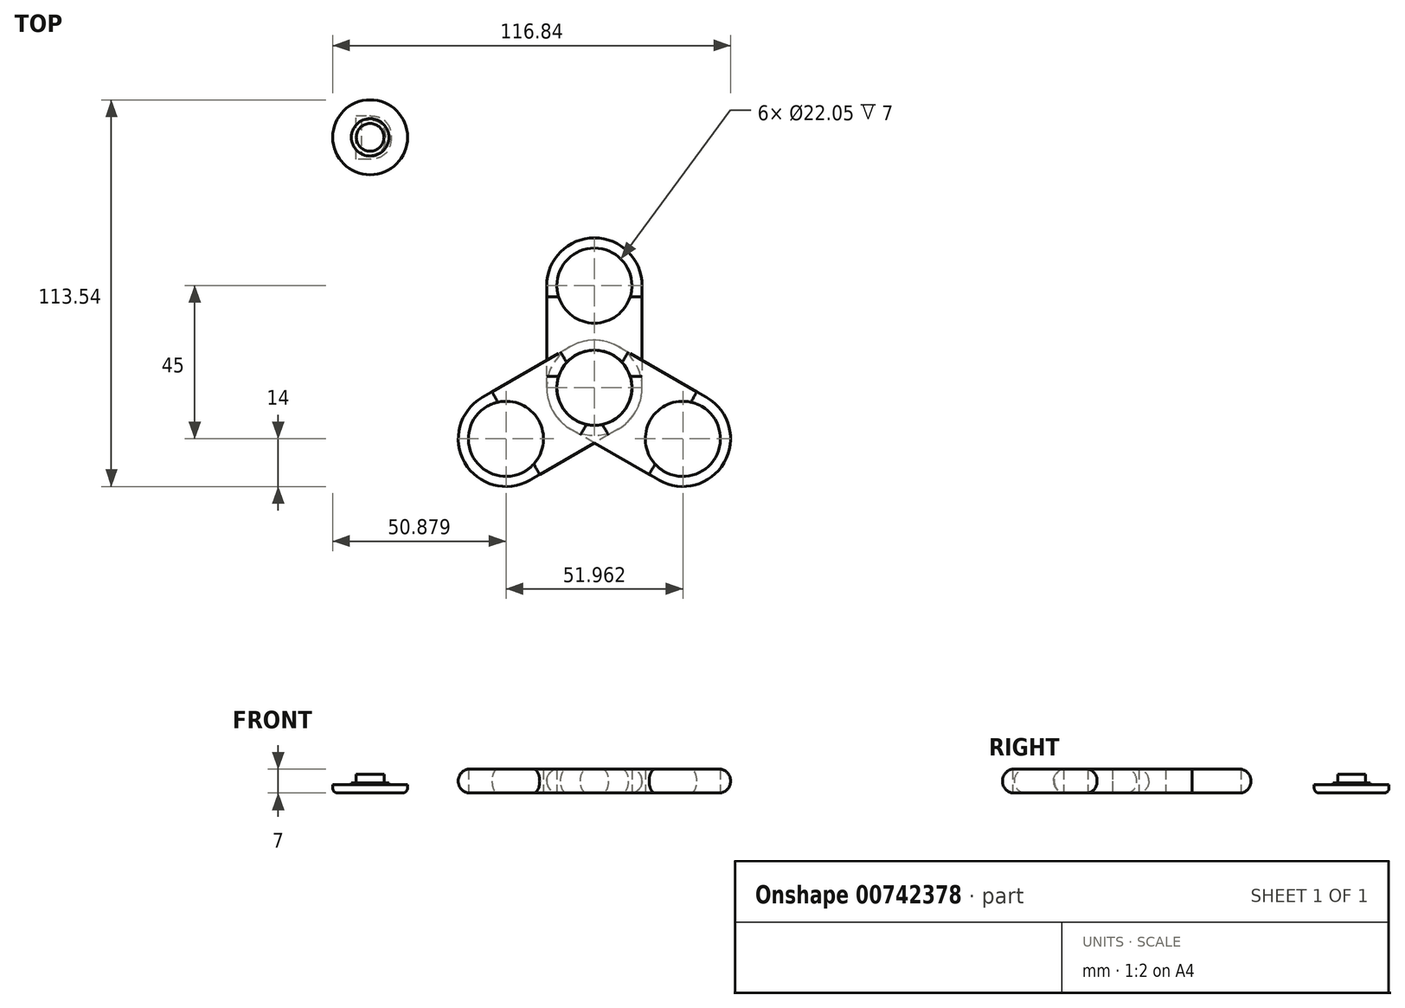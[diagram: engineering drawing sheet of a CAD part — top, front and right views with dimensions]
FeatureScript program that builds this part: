
annotation { "Feature Type Name" : "Feature", "Feature Type Description" : "" }
export const myFeature = defineFeature(function(context is Context, id is Id, definition is map)
    precondition{}
    {
        {
            var Q0;
            Q0=qCreatedBy(makeId("Top.planeOp"),FACE);
            var sketch = newSketch(context, id + "F0", { "sketchPlane" : qUnion([Q0])});
            skLineSegment(sketch, "E0.bottom", {"start": v(0, 0) * mm, "end": v(28, 0) * mm});
            skLineSegment(sketch, "E0.top", {"start": v(0, -30) * mm, "end": v(28, -30) * mm});
            skLineSegment(sketch, "E0.left", {"start": v(0, 0) * mm, "end": v(0, -30) * mm});
            skLineSegment(sketch, "E0.right", {"start": v(28, 0) * mm, "end": v(28, -30) * mm});
            skCircle(sketch, "E1", {"center": v(14, 0) * mm, "radius": 14 * mm});
            skCircle(sketch, "E2", {"center": v(14, 0) * mm, "radius": 11.03 * mm});
            skCircle(sketch, "E3", {"center": v(14, -30) * mm, "radius": 14 * mm});
            skCircle(sketch, "E4", {"center": v(14, -30) * mm, "radius": 11.03 * mm});
            skSolve(sketch);
        }
        {
            var Q0;
            {var subQ1=sQuery(id+"F0.wireOp",EDGE,"E0.top");var subQ3=sQuery(id+"F0.wireOp",EDGE,"E4");var subQ4=makeQuery(id+"F0.imprint","INTERSECT",VERTEX,{"disambiguationData":[OD(0.0)],"derivedFrom":[subQ1,subQ3]});Q0=makeQuery(id+"F0.imprint","IMPRINT",FACE,{"disambiguationData":[TD([[makeQuery(id+"F0.imprint","IMPRINT",EDGE,{"disambiguationData":[TD([[subQ4,-1.0]])],"derivedFrom":subQ3}),-1.0]])]});}
            var Q1;
            {var subQ1=sQuery(id+"F0.wireOp",EDGE,"E0.bottom");var subQ3=sQuery(id+"F0.wireOp",EDGE,"E2");var subQ4=makeQuery(id+"F0.imprint","INTERSECT",VERTEX,{"disambiguationData":[OD(0.0)],"derivedFrom":[subQ1,subQ3]});Q1=makeQuery(id+"F0.imprint","IMPRINT",FACE,{"disambiguationData":[TD([[makeQuery(id+"F0.imprint","IMPRINT",EDGE,{"disambiguationData":[TD([[subQ4,-1.0]])],"derivedFrom":subQ3}),-1.0]])]});}
            var Q2;
            {var subQ1=sQuery(id+"F0.wireOp",EDGE,"E0.top");var subQ3=sQuery(id+"F0.wireOp",EDGE,"E4");var subQ4=makeQuery(id+"F0.imprint","INTERSECT",VERTEX,{"disambiguationData":[OD(0.0)],"derivedFrom":[subQ1,subQ3]});Q2=makeQuery(id+"F0.imprint","IMPRINT",FACE,{"disambiguationData":[TD([[makeQuery(id+"F0.imprint","IMPRINT",EDGE,{"disambiguationData":[TD([[subQ4,1.0]])],"derivedFrom":subQ3}),-1.0]])]});}
            var Q3;
            {var subQ1=sQuery(id+"F0.wireOp",EDGE,"E0.bottom");var subQ3=sQuery(id+"F0.wireOp",EDGE,"E2");var subQ4=makeQuery(id+"F0.imprint","INTERSECT",VERTEX,{"disambiguationData":[OD(0.0)],"derivedFrom":[subQ1,subQ3]});Q3=makeQuery(id+"F0.imprint","IMPRINT",FACE,{"disambiguationData":[TD([[makeQuery(id+"F0.imprint","IMPRINT",EDGE,{"disambiguationData":[TD([[subQ4,1.0]])],"derivedFrom":subQ3}),-1.0]])]});}
            var Q4;
            {var subQ0=sQuery(id+"F0.wireOp",EDGE,"E0.left");Q4=makeQuery(id+"F0.imprint","IMPRINT",FACE,{"disambiguationData":[TD([[makeQuery(id+"F0.imprint","IMPRINT",EDGE,{"derivedFrom":subQ0}),1.0]])]});}
            extrude(context, id + "F1", {"entities" : qUnion([Q0, Q1, Q2, Q3, Q4]), "depth" : 7 * mm, "offsetDistance" : 25 * mm});
        }
        {
            var Q0;
            Q0=makeQuery(id+"F1.opExtrude","SWEPT_BODY",BODY,{"disambiguationData":[OSD([sQuery(id+"F0.wireOp",EDGE,"E0.left"),sQuery(id+"F0.wireOp",EDGE,"E0.right"),sQuery(id+"F0.wireOp",EDGE,"E1"),sQuery(id+"F0.wireOp",EDGE,"E2"),sQuery(id+"F0.wireOp",EDGE,"E3"),sQuery(id+"F0.wireOp",EDGE,"E4")])]});
            var Q1;
            Q1=makeQuery(id+"F1.opExtrude","SWEPT_FACE",FACE,{"disambiguationData":[OSD([sQuery(id+"F0.wireOp",EDGE,"E3")])]});
            circularPattern(context, id + "F2", {"entities" : qUnion([Q0]), "axis" : qUnion([Q1]), "angle" : 360 * degree, "instanceCount" : 3, "equalSpace" : true});
        }
        {
            var Q0;
            Q0=qCreatedBy(makeId("Top.planeOp"),FACE);
            var sketch = newSketch(context, id + "F3", { "sketchPlane" : qUnion([Q0])});
            skCircle(sketch, "E5", {"center": v(-51.86, 43.54) * mm, "radius": 11 * mm});
            skCircle(sketch, "E6", {"center": v(-51.86, 43.54) * mm, "radius": 5.5 * mm});
            skCircle(sketch, "E7", {"center": v(-51.86, 43.54) * mm, "radius": 4.08 * mm});
            skSolve(sketch);
        }
        {
            var Q0;
            Q0=makeQuery(id+"F3.imprint","IMPRINT",FACE,{"disambiguationData":[TD([[makeQuery(id+"F3.imprint","IMPRINT",EDGE,{"derivedFrom":sQuery(id+"F3.wireOp",EDGE,"E5")}),1.0]])]});
            extrude(context, id + "F4", {"entities" : qUnion([Q0]), "depth" : 2.5 * mm, "offsetDistance" : 25 * mm});
        }
        {
            var Q0;
            Q0=makeQuery(id+"F3.imprint","IMPRINT",FACE,{"disambiguationData":[TD([[makeQuery(id+"F3.imprint","IMPRINT",EDGE,{"derivedFrom":sQuery(id+"F3.wireOp",EDGE,"E6")}),1.0]])]});
            extrude(context, id + "F5", {"entities" : qUnion([Q0]), "operationType" : NewBodyOperationType.ADD, "depth" : 3 * mm, "offsetDistance" : 25 * mm});
        }
        {
            var Q0;
            Q0=makeQuery(id+"F3.imprint","IMPRINT",FACE,{"disambiguationData":[TD([[makeQuery(id+"F3.imprint","IMPRINT",EDGE,{"derivedFrom":sQuery(id+"F3.wireOp",EDGE,"E7")}),1.0]])]});
            extrude(context, id + "F6", {"entities" : qUnion([Q0]), "operationType" : NewBodyOperationType.ADD, "depth" : 5.5 * mm, "offsetDistance" : 25 * mm});
        }
        {
            var Q0;
            Q0=makeQuery(id+"F2.opPattern","COPY",EDGE,{"derivedFrom":makeQuery(id+"F1.opExtrude","CAP_EDGE",EDGE,{"disambiguationData":[OSD([sQuery(id+"F0.wireOp",EDGE,"E0.left")])],"isStart":false}),"instanceName":"2"});
            var Q1;
            Q1=makeQuery(id+"F2.opPattern","COPY",EDGE,{"derivedFrom":makeQuery(id+"F1.opExtrude","CAP_EDGE",EDGE,{"disambiguationData":[OSD([sQuery(id+"F0.wireOp",EDGE,"E1")])],"isStart":false}),"instanceName":"2"});
            var Q2;
            Q2=makeQuery(id+"F2.opPattern","COPY",EDGE,{"derivedFrom":makeQuery(id+"F1.opExtrude","CAP_EDGE",EDGE,{"disambiguationData":[OSD([sQuery(id+"F0.wireOp",EDGE,"E0.right")])],"isStart":false}),"instanceName":"2"});
            var Q3;
            Q3=makeQuery(id+"F1.opExtrude","CAP_EDGE",EDGE,{"disambiguationData":[OSD([sQuery(id+"F0.wireOp",EDGE,"E0.left")])],"isStart":false});
            var Q4;
            Q4=makeQuery(id+"F1.opExtrude","CAP_EDGE",EDGE,{"disambiguationData":[OSD([sQuery(id+"F0.wireOp",EDGE,"E1")])],"isStart":false});
            var Q5;
            Q5=makeQuery(id+"F1.opExtrude","CAP_EDGE",EDGE,{"disambiguationData":[OSD([sQuery(id+"F0.wireOp",EDGE,"E0.right")])],"isStart":false});
            var Q6;
            Q6=makeQuery(id+"F2.opPattern","COPY",EDGE,{"derivedFrom":makeQuery(id+"F1.opExtrude","CAP_EDGE",EDGE,{"disambiguationData":[OSD([sQuery(id+"F0.wireOp",EDGE,"E0.left")])],"isStart":false}),"instanceName":"1"});
            var Q7;
            Q7=makeQuery(id+"F2.opPattern","COPY",EDGE,{"derivedFrom":makeQuery(id+"F1.opExtrude","CAP_EDGE",EDGE,{"disambiguationData":[OSD([sQuery(id+"F0.wireOp",EDGE,"E1")])],"isStart":false}),"instanceName":"1"});
            var Q8;
            Q8=makeQuery(id+"F2.opPattern","COPY",EDGE,{"derivedFrom":makeQuery(id+"F1.opExtrude","CAP_EDGE",EDGE,{"disambiguationData":[OSD([sQuery(id+"F0.wireOp",EDGE,"E0.right")])],"isStart":false}),"instanceName":"1"});
            fillet(context, id + "F7", {"entities" : qUnion([Q0, Q1, Q2, Q3, Q4, Q5, Q6, Q7, Q8]), "radius" : 3.5 * mm, "tangentPropagation" : true, "allowEdgeOverflow" : false});
        }
        {
            var Q0;
            Q0=makeQuery(id+"F2.opPattern","COPY",EDGE,{"derivedFrom":makeQuery(id+"F1.opExtrude","CAP_EDGE",EDGE,{"disambiguationData":[OSD([sQuery(id+"F0.wireOp",EDGE,"E0.left")])],"isStart":true}),"instanceName":"2"});
            var Q1;
            Q1=makeQuery(id+"F2.opPattern","COPY",EDGE,{"derivedFrom":makeQuery(id+"F1.opExtrude","CAP_EDGE",EDGE,{"disambiguationData":[OSD([sQuery(id+"F0.wireOp",EDGE,"E1")])],"isStart":true}),"instanceName":"2"});
            var Q2;
            Q2=makeQuery(id+"F2.opPattern","COPY",EDGE,{"derivedFrom":makeQuery(id+"F1.opExtrude","CAP_EDGE",EDGE,{"disambiguationData":[OSD([sQuery(id+"F0.wireOp",EDGE,"E0.right")])],"isStart":true}),"instanceName":"2"});
            var Q3;
            Q3=makeQuery(id+"F1.opExtrude","CAP_EDGE",EDGE,{"disambiguationData":[OSD([sQuery(id+"F0.wireOp",EDGE,"E0.left")])],"isStart":true});
            var Q4;
            Q4=makeQuery(id+"F1.opExtrude","CAP_EDGE",EDGE,{"disambiguationData":[OSD([sQuery(id+"F0.wireOp",EDGE,"E1")])],"isStart":true});
            var Q5;
            Q5=makeQuery(id+"F1.opExtrude","CAP_EDGE",EDGE,{"disambiguationData":[OSD([sQuery(id+"F0.wireOp",EDGE,"E0.right")])],"isStart":true});
            var Q6;
            Q6=makeQuery(id+"F2.opPattern","COPY",EDGE,{"derivedFrom":makeQuery(id+"F1.opExtrude","CAP_EDGE",EDGE,{"disambiguationData":[OSD([sQuery(id+"F0.wireOp",EDGE,"E0.left")])],"isStart":true}),"instanceName":"1"});
            var Q7;
            Q7=makeQuery(id+"F2.opPattern","COPY",EDGE,{"derivedFrom":makeQuery(id+"F1.opExtrude","CAP_EDGE",EDGE,{"disambiguationData":[OSD([sQuery(id+"F0.wireOp",EDGE,"E1")])],"isStart":true}),"instanceName":"1"});
            var Q8;
            Q8=makeQuery(id+"F2.opPattern","COPY",EDGE,{"derivedFrom":makeQuery(id+"F1.opExtrude","CAP_EDGE",EDGE,{"disambiguationData":[OSD([sQuery(id+"F0.wireOp",EDGE,"E0.right")])],"isStart":true}),"instanceName":"1"});
            fillet(context, id + "F8", {"entities" : qUnion([Q0, Q1, Q2, Q3, Q4, Q5, Q6, Q7, Q8]), "radius" : 3.5 * mm, "tangentPropagation" : true, "allowEdgeOverflow" : false});
        }
        {
            var Q0;
            Q0=makeQuery(id+"F4.opExtrude","CAP_EDGE",EDGE,{"disambiguationData":[OSD([sQuery(id+"F3.wireOp",EDGE,"E5")])],"isStart":true});
            fillet(context, id + "F9", {"entities" : qUnion([Q0]), "radius" : 1.5 * mm, "tangentPropagation" : true, "allowEdgeOverflow" : false});
        }
        {
            var Q0;
            Q0=qCreatedBy(makeId("Top.planeOp"),FACE);
            var sketch = newSketch(context, id + "F10", { "sketchPlane" : qUnion([Q0])});
            skText(sketch, "E8", { "text": "D", "fontName": "OpenSans-Regular.ttf"});
            const initialGuessF10  = {"E8": [-0.05769, 0.03703, 1, 0, 0.01294]};
            skSetInitialGuess(sketch, initialGuessF10);
            skSolve(sketch);
        }
        {
            var Q0;
            Q0=makeQuery(id+"F10.imprint","IMPRINT",FACE,{"disambiguationData":[TD([[makeQuery(id+"F10.imprint","IMPRINT",EDGE,{"derivedFrom":sQuery(id+"F10.wireOp",EDGE,"E8.sketch_text.stroke-0")}),-1.0]])]});
            extrude(context, id + "F11", {"entities" : qUnion([Q0]), "operationType" : NewBodyOperationType.REMOVE, "depth" : .15 * mm, "offsetDistance" : 25 * mm});
        }
    });
